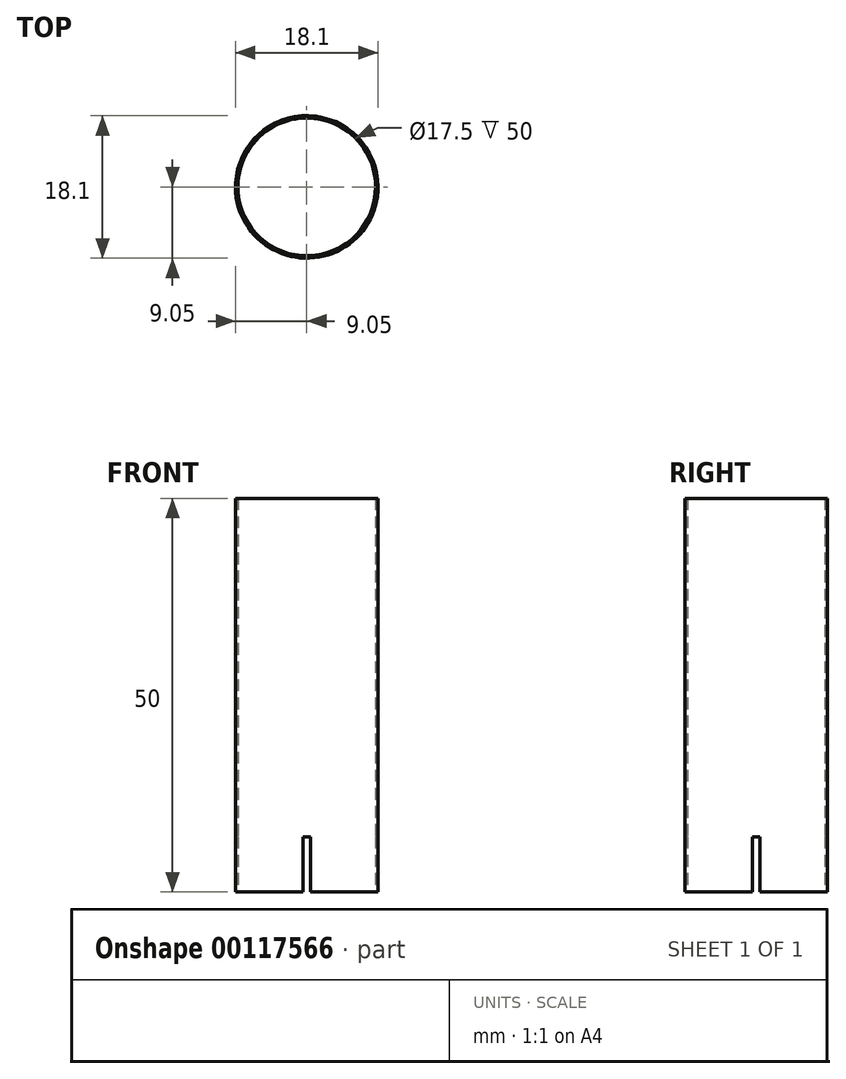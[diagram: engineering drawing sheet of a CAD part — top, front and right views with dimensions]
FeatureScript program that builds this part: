
annotation { "Feature Type Name" : "Feature", "Feature Type Description" : "" }
export const myFeature = defineFeature(function(context is Context, id is Id, definition is map)
    precondition{}
    {
        {
            var Q0;
            Q0=qCreatedBy(makeId("Top.planeOp"),FACE);
            var sketch = newSketch(context, id + "F0", { "sketchPlane" : qUnion([Q0])});
            skCircle(sketch, "E0", {"center": v(0, 0) * mm, "radius": 8.75 * mm});
            skCircle(sketch, "E1", {"center": v(0, 0) * mm, "radius": 9.05 * mm});
            skSolve(sketch);
        }
        {
            var Q0;
            Q0 = qSketchRegion(id + "F0", true);
            extrude(context, id + "F1", {"entities" : qUnion([Q0]), "depth" : 50 * mm});
        }
        {
            var Q0;
            Q0=qCreatedBy(makeId("Top.planeOp"),FACE);
            var sketch = newSketch(context, id + "F2", { "sketchPlane" : qUnion([Q0])});
            skLineSegment(sketch, "E2.bottom", {"start": v(-0.5, 9.05) * mm, "end": v(0.5, 9.05) * mm});
            skLineSegment(sketch, "E2.top", {"start": v(-0.5, -9.05) * mm, "end": v(0.5, -9.05) * mm});
            skLineSegment(sketch, "E2.left", {"start": v(-0.5, 9.05) * mm, "end": v(-0.5, -9.05) * mm});
            skLineSegment(sketch, "E2.right", {"start": v(0.5, 9.05) * mm, "end": v(0.5, -9.05) * mm});
            skLineSegment(sketch, "E3", {"start": v(-0.5, 0) * mm, "end": v(0.5, 0) * mm});
            skSolve(sketch);
        }
        {
            var Q0;
            Q0 = qSketchRegion(id + "F2", true);
            extrude(context, id + "F3", {"entities" : qUnion([Q0]), "depth" : 7 * mm});
        }
        {
            var Q0;
            Q0=makeQuery(id+"F3.opExtrude","SWEPT_BODY",BODY,{"disambiguationData":[OSD([sQuery(id+"F2.wireOp",EDGE,"E2.bottom"),sQuery(id+"F2.wireOp",EDGE,"E2.top"),sQuery(id+"F2.wireOp",EDGE,"E2.left"),sQuery(id+"F2.wireOp",EDGE,"E2.right")])]});
            var Q1;
            Q1=makeQuery(id+"F1.opExtrude","SWEPT_FACE",FACE,{"disambiguationData":[OSD([sQuery(id+"F0.wireOp",EDGE,"E1")])]});
            circularPattern(context, id + "F4", {"entities" : qUnion([Q0]), "axis" : qUnion([Q1]), "angle" : 90 * degree, "instanceCount" : 2, "computeTransformsWithoutBuiltin" : true});
        }
        {
            var Q0;
            Q0=makeQuery(id+"F3.opExtrude","SWEPT_BODY",BODY,{"disambiguationData":[OSD([sQuery(id+"F2.wireOp",EDGE,"E2.bottom"),sQuery(id+"F2.wireOp",EDGE,"E2.top"),sQuery(id+"F2.wireOp",EDGE,"E2.left"),sQuery(id+"F2.wireOp",EDGE,"E2.right")])]});
            var Q1;
            Q1=makeQuery(id+"F4.opPattern","COPY",BODY,{"derivedFrom":makeQuery(id+"F3.opExtrude","SWEPT_BODY",BODY,{"disambiguationData":[OSD([sQuery(id+"F2.wireOp",EDGE,"E2.bottom"),sQuery(id+"F2.wireOp",EDGE,"E2.top"),sQuery(id+"F2.wireOp",EDGE,"E2.left"),sQuery(id+"F2.wireOp",EDGE,"E2.right")])]}),"instanceName":"1"});
            var Q2;
            Q2=makeQuery(id+"F1.opExtrude","SWEPT_BODY",BODY,{"disambiguationData":[OSD([sQuery(id+"F0.wireOp",EDGE,"E0"),sQuery(id+"F0.wireOp",EDGE,"E1")])]});
            booleanBodies(context, id + "F5", {"operationType" : BooleanOperationType.SUBTRACTION, "tools" : qUnion([Q0, Q1]), "targets" : qUnion([Q2])});
        }
    });
